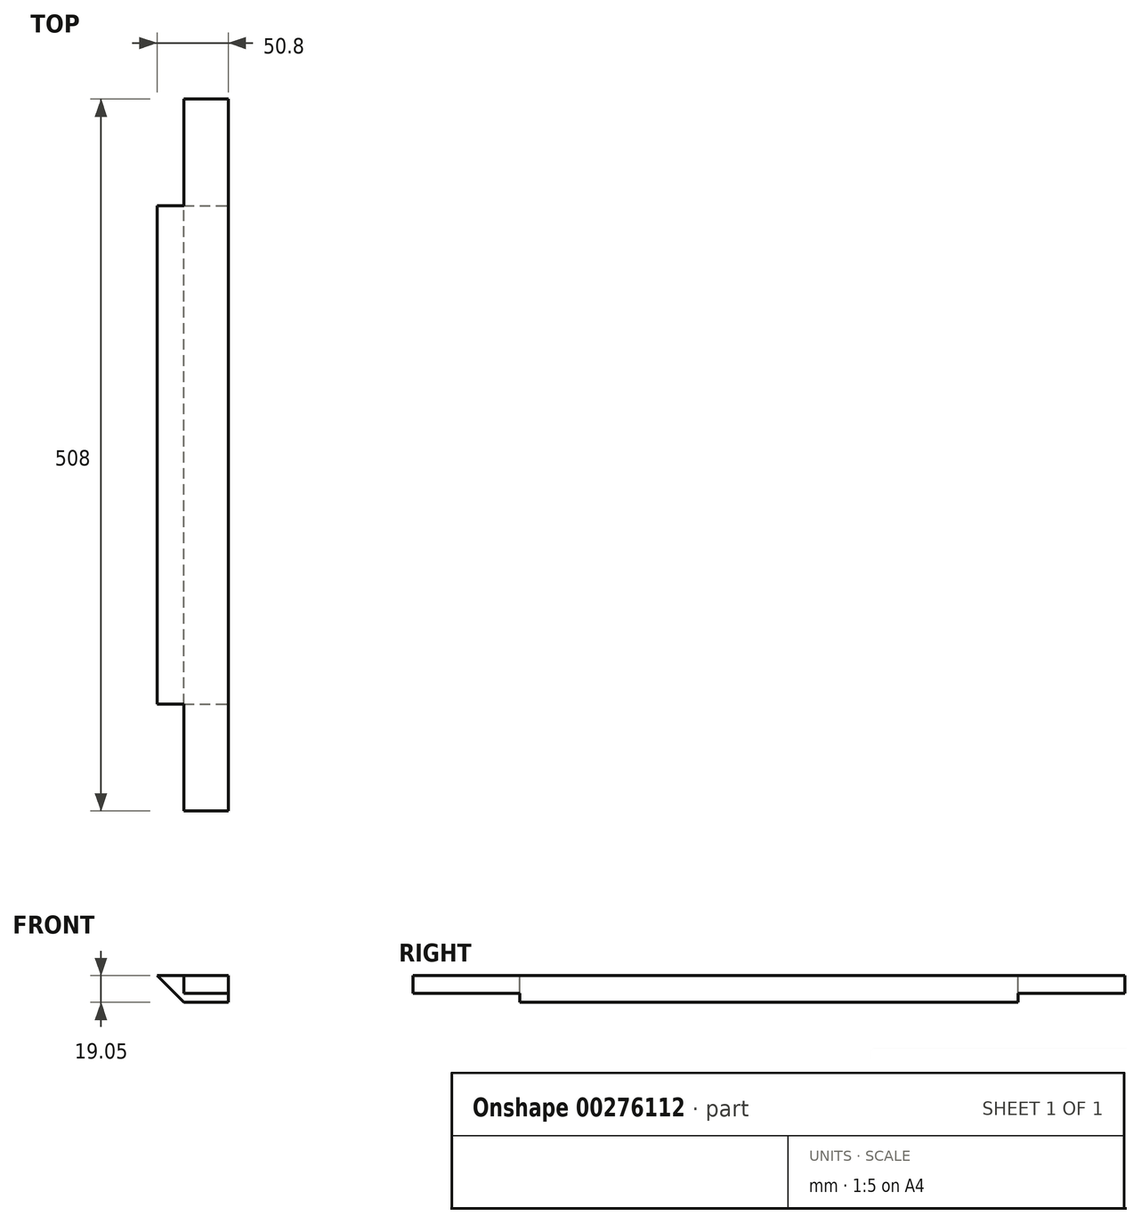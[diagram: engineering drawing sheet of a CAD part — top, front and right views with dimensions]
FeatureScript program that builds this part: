
annotation { "Feature Type Name" : "Feature", "Feature Type Description" : "" }
export const myFeature = defineFeature(function(context is Context, id is Id, definition is map)
    precondition{}
    {
        {
            var Q0;
            Q0=qCreatedBy(makeId("Front.planeOp"),FACE);
            var sketch = newSketch(context, id + "F0", { "sketchPlane" : qUnion([Q0])});
            skLineSegment(sketch, "E0", {"start": v(0, 0) * mm, "end": v(0, -19.05) * mm});
            skLineSegment(sketch, "E1", {"start": v(0, -19.05) * mm, "end": v(-31.75, -19.05) * mm});
            skLineSegment(sketch, "E2", {"start": v(-31.75, -19.05) * mm, "end": v(-50.8, 0) * mm});
            skLineSegment(sketch, "E3", {"start": v(-50.8, 0) * mm, "end": v(0, 0) * mm});
            skSolve(sketch);
        }
        {
            var Q0;
            Q0=makeQuery(id+"F0.imprint","IMPRINT",FACE,{"disambiguationData":[TD([[makeQuery(id+"F0.imprint","IMPRINT",EDGE,{"derivedFrom":sQuery(id+"F0.wireOp",EDGE,"E0")}),-1.0]])]});
            extrude(context, id + "F1", {"entities" : qUnion([Q0]), "depth" : 508 * mm});
        }
        {
            var Q0;
            Q0=makeQuery(id+"F1.opExtrude","SWEPT_FACE",FACE,{"disambiguationData":[OSD([sQuery(id+"F0.wireOp",EDGE,"E3")])]});
            var sketch = newSketch(context, id + "F2", { "sketchPlane" : qUnion([Q0])});
            skLineSegment(sketch, "E4.bottom", {"start": v(-50.8, 0) * mm, "end": v(-31.75, 0) * mm});
            skLineSegment(sketch, "E4.top", {"start": v(-50.8, -76.2) * mm, "end": v(-31.75, -76.2) * mm});
            skLineSegment(sketch, "E4.left", {"start": v(-50.8, 0) * mm, "end": v(-50.8, -76.2) * mm});
            skLineSegment(sketch, "E4.right", {"start": v(-31.75, 0) * mm, "end": v(-31.75, -76.2) * mm});
            skLineSegment(sketch, "E5.bottom", {"start": v(-50.8, -508) * mm, "end": v(-31.75, -508) * mm});
            skLineSegment(sketch, "E5.top", {"start": v(-50.8, -431.8) * mm, "end": v(-31.75, -431.8) * mm});
            skLineSegment(sketch, "E5.left", {"start": v(-50.8, -508) * mm, "end": v(-50.8, -431.8) * mm});
            skLineSegment(sketch, "E5.right", {"start": v(-31.75, -508) * mm, "end": v(-31.75, -431.8) * mm});
            skSolve(sketch);
        }
        {
            var Q0;
            Q0 = qSketchRegion(id + "F2", true);
            extrude(context, id + "F3", {"entities" : qUnion([Q0]), "operationType" : NewBodyOperationType.REMOVE, "oppositeDirection" : true, "depth" : 25.4 * mm});
        }
        {
            var Q0;
            Q0=makeQuery(id+"F1.opExtrude","SWEPT_FACE",FACE,{"disambiguationData":[OSD([sQuery(id+"F0.wireOp",EDGE,"E0")])]});
            var sketch = newSketch(context, id + "F4", { "sketchPlane" : qUnion([Q0])});
            skLineSegment(sketch, "E6.bottom", {"start": v(-508, -19.05) * mm, "end": v(-431.8, -19.05) * mm});
            skLineSegment(sketch, "E6.top", {"start": v(-508, -12.7) * mm, "end": v(-431.8, -12.7) * mm});
            skLineSegment(sketch, "E6.left", {"start": v(-508, -19.05) * mm, "end": v(-508, -12.7) * mm});
            skLineSegment(sketch, "E6.right", {"start": v(-431.8, -19.05) * mm, "end": v(-431.8, -12.7) * mm});
            skLineSegment(sketch, "E7.bottom", {"start": v(0, -19.05) * mm, "end": v(-76.2, -19.05) * mm});
            skLineSegment(sketch, "E7.top", {"start": v(0, -12.7) * mm, "end": v(-76.2, -12.7) * mm});
            skLineSegment(sketch, "E7.left", {"start": v(0, -19.05) * mm, "end": v(0, -12.7) * mm});
            skLineSegment(sketch, "E7.right", {"start": v(-76.2, -19.05) * mm, "end": v(-76.2, -12.7) * mm});
            skSolve(sketch);
        }
        {
            var Q0;
            Q0=makeQuery(id+"F4.imprint","IMPRINT",FACE,{"disambiguationData":[TD([[makeQuery(id+"F4.imprint","IMPRINT",EDGE,{"derivedFrom":sQuery(id+"F4.wireOp",EDGE,"E6.bottom")}),1.0]])]});
            var Q1;
            Q1=makeQuery(id+"F4.imprint","IMPRINT",FACE,{"disambiguationData":[TD([[makeQuery(id+"F4.imprint","IMPRINT",EDGE,{"derivedFrom":sQuery(id+"F4.wireOp",EDGE,"E7.bottom")}),1.0]])]});
            extrude(context, id + "F5", {"entities" : qUnion([Q0, Q1]), "operationType" : NewBodyOperationType.REMOVE, "endBound" : BoundingType.THROUGH_ALL, "oppositeDirection" : true, "depth" : 25.4 * mm});
        }
    });
